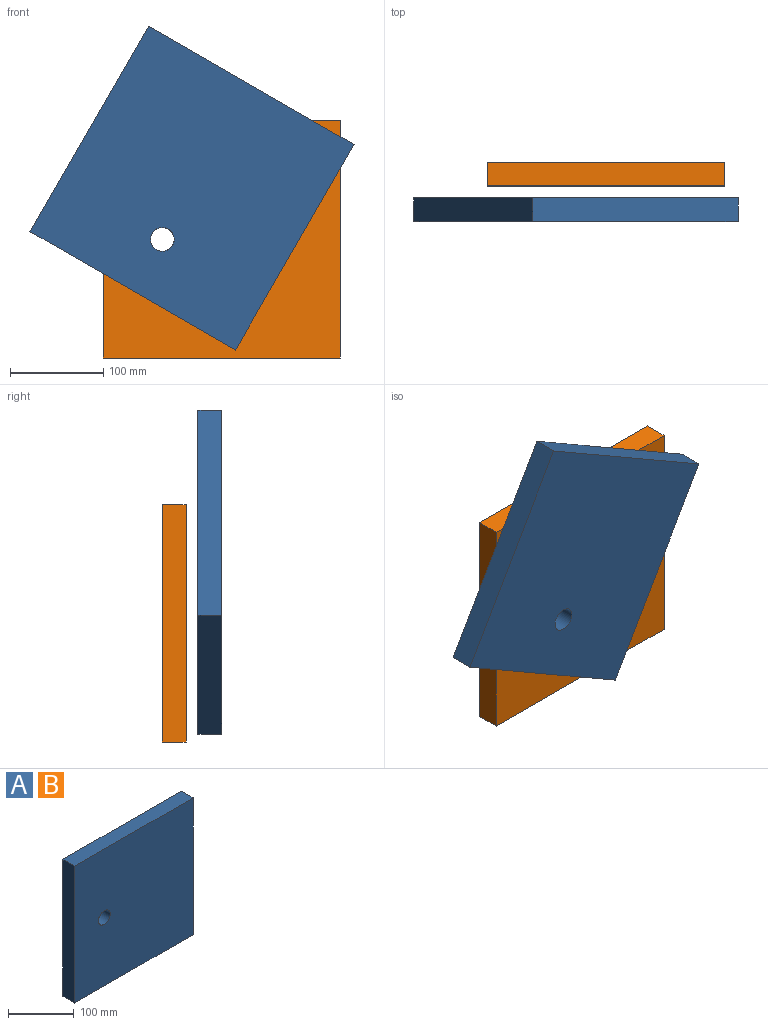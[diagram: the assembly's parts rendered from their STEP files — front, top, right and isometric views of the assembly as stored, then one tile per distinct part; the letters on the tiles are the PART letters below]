
ASSEMBLY  parts=2 mates=1
PART A: 7 faces, bbox 254x25.4x254 mm
  f0: plane 254x25.4mm, normal (-1,0,0), area 6451.6mm2, adj f1,f3,f5,f6
  f1: plane 254x25.4mm, normal (0,0,-1), area 6451.6mm2, adj f0,f2,f5,f6
  f2: plane 254x25.4mm, normal (1,0,0), area 6451.6mm2, adj f1,f3,f5,f6
  f3: plane 254x25.4mm, normal (0,0,1), area 6451.6mm2, adj f0,f2,f5,f6
  f4: cylinder r=12.7mm len=25.4mm, axis (0,1,0), area 2026.8mm2, adj f5,f6
  f5: plane 254x254mm, normal (0,-1,0), area 64009.3mm2, adj f0,f1,f2,f3,f4
  f6: plane 254x254mm, normal (0,1,0), area 64009.3mm2, adj f0,f1,f2,f3,f4
PART B: same geometry as A
PLACE A rot(axis=(0,-1,0),60deg) t=(14.23,-12.7,-118.49)mm
PLACE B t=(-127.5,25.4,-127)mm fixed
MATE cylindrical B.f4 <-> A.f4  axis (0,1,0) through (-64,0,0)mm
